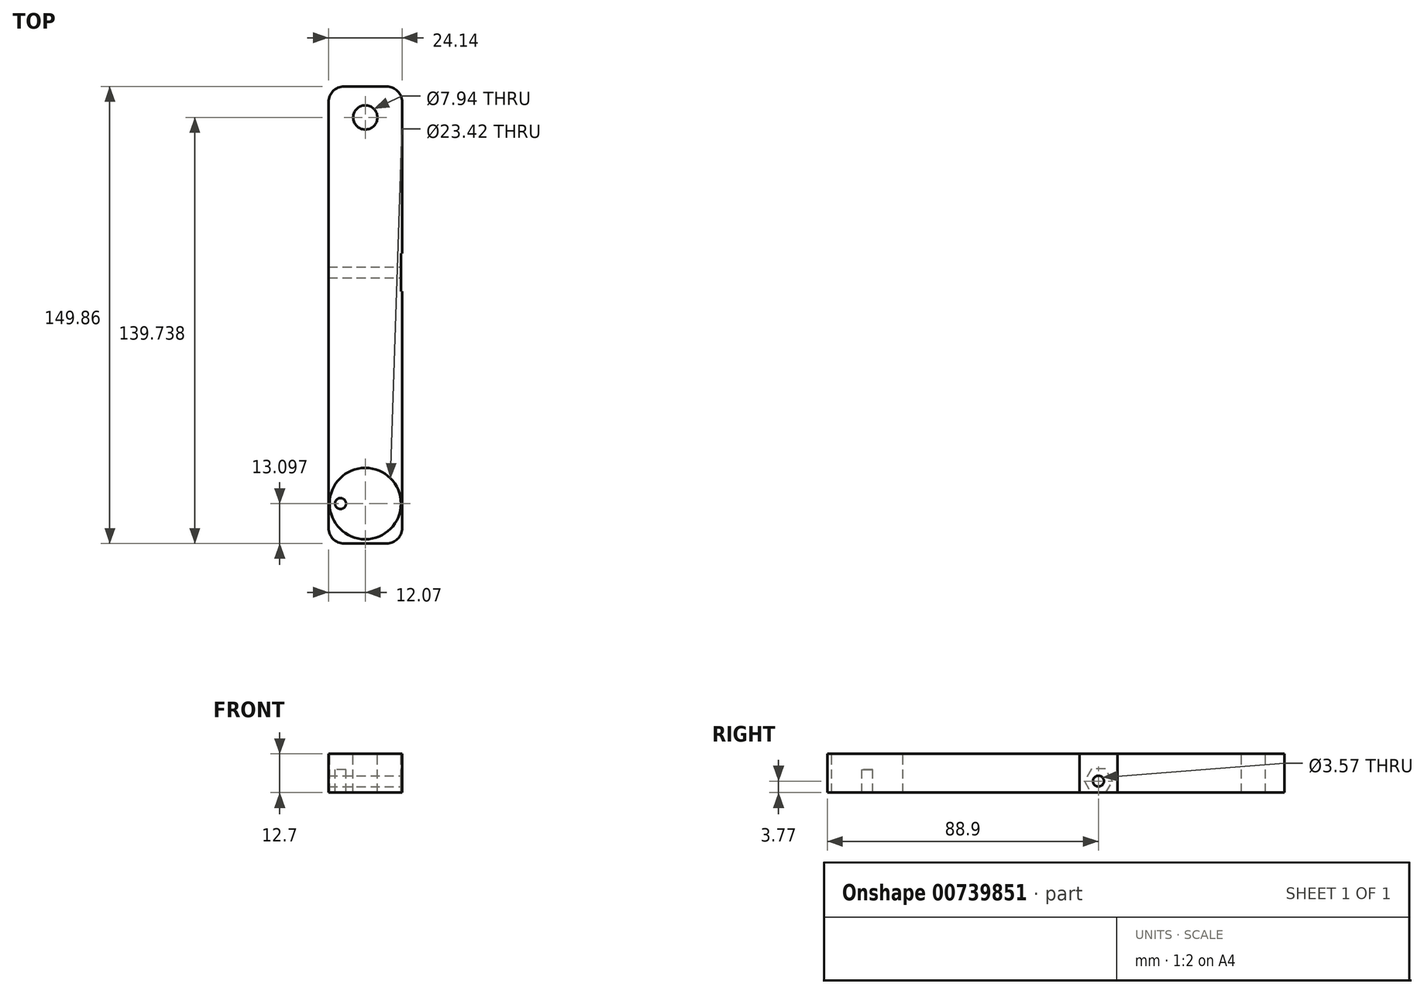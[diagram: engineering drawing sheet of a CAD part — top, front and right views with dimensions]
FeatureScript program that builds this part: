
annotation { "Feature Type Name" : "Feature", "Feature Type Description" : "" }
export const myFeature = defineFeature(function(context is Context, id is Id, definition is map)
    precondition{}
    {
        {
            var Q0;
            Q0=qCreatedBy(makeId("Top.planeOp"),FACE);
            var sketch = newSketch(context, id + "F0", { "sketchPlane" : qUnion([Q0])});
            skLineSegment(sketch, "E0.bottom", {"start": v(12.07, -88.9) * mm, "end": v(-12.06, -88.9) * mm});
            skLineSegment(sketch, "E0.top", {"start": v(12.06, 60.96) * mm, "end": v(-12.07, 60.96) * mm});
            skLineSegment(sketch, "E0.left", {"start": v(12.07, -88.9) * mm, "end": v(12.06, 60.96) * mm});
            skLineSegment(sketch, "E0.right", {"start": v(-12.06, -88.9) * mm, "end": v(-12.07, 60.96) * mm});
            skSolve(sketch);
        }
        {
            var Q0;
            Q0=makeQuery(id+"F0.imprint","IMPRINT",FACE,{"disambiguationData":[TD([[makeQuery(id+"F0.imprint","IMPRINT",EDGE,{"derivedFrom":sQuery(id+"F0.wireOp",EDGE,"E0.bottom")}),-1.0]])]});
            extrude(context, id + "F1", {"entities" : qUnion([Q0]), "depth" : 12.7 * mm, "offsetDistance" : 25.4 * mm});
        }
        {
            var Q0;
            Q0=makeQuery(id+"F1.opExtrude","SWEPT_FACE",FACE,{"disambiguationData":[OSD([sQuery(id+"F0.wireOp",EDGE,"E0.left")])]});
            var sketch = newSketch(context, id + "F2", { "sketchPlane" : qUnion([Q0])});
            skLineSegment(sketch, "E1.bottom", {"start": v(6.22, 12.7) * mm, "end": v(-6.22, 12.7) * mm});
            skLineSegment(sketch, "E1.top", {"start": v(6.22, -7.62) * mm, "end": v(-6.22, -7.62) * mm});
            skLineSegment(sketch, "E1.left", {"start": v(6.22, 12.7) * mm, "end": v(6.22, -7.62) * mm});
            skLineSegment(sketch, "E1.right", {"start": v(-6.22, 12.7) * mm, "end": v(-6.22, -7.62) * mm});
            skSolve(sketch);
        }
        {
            var Q0;
            Q0 = qSketchRegion(id + "F2", true);
            extrude(context, id + "F3", {"entities" : qUnion([Q0]), "operationType" : NewBodyOperationType.REMOVE, "oppositeDirection" : true, "depth" : 0.3 * mm, "offsetDistance" : 25.4 * mm});
        }
        {
            var Q0;
            Q0=makeQuery(id+"F1.opExtrude","CAP_FACE",FACE,{"disambiguationData":[OSD([sQuery(id+"F0.wireOp",EDGE,"E0.bottom"),sQuery(id+"F0.wireOp",EDGE,"E0.top"),sQuery(id+"F0.wireOp",EDGE,"E0.left"),sQuery(id+"F0.wireOp",EDGE,"E0.right")])],"isStart":false});
            var sketch = newSketch(context, id + "F4", { "sketchPlane" : qUnion([Q0])});
            skCircle(sketch, "E2", {"center": v(1.59, 51.33) * mm, "radius": 1.59 * mm, "construction": true});
            skCircle(sketch, "E3.MirrorC", {"center": v(-1.59, 51.33) * mm, "radius": 1.59 * mm, "construction": true});
            skCircle(sketch, "E4", {"center": v(0, 48.58) * mm, "radius": 1.59 * mm, "construction": true});
            skCircle(sketch, "E5", {"center": v(0, 50.84) * mm, "radius": 3.97 * mm});
            skSolve(sketch);
        }
        {
            var Q0;
            Q0 = qSketchRegion(id + "F4", true);
            extrude(context, id + "F5", {"entities" : qUnion([Q0]), "operationType" : NewBodyOperationType.REMOVE, "oppositeDirection" : true, "depth" : 25.4 * mm, "offsetDistance" : 25.4 * mm});
        }
        {
            var Q0;
            Q0=makeQuery(id+"F1.opExtrude","CAP_FACE",FACE,{"disambiguationData":[OSD([sQuery(id+"F0.wireOp",EDGE,"E0.bottom"),sQuery(id+"F0.wireOp",EDGE,"E0.top"),sQuery(id+"F0.wireOp",EDGE,"E0.left"),sQuery(id+"F0.wireOp",EDGE,"E0.right")])],"isStart":false});
            var sketch = newSketch(context, id + "F6", { "sketchPlane" : qUnion([Q0])});
            skCircle(sketch, "E6", {"center": v(0, -75.8) * mm, "radius": 11.7 * mm});
            skCircle(sketch, "E7", {"center": v(0, 0) * mm, "radius": 44.45 * mm, "construction": true});
            skLineSegment(sketch, "E8", {"start": v(0, -44.45) * mm, "end": v(60.85, -44.45) * mm, "construction": true});
            skSolve(sketch);
        }
        {
            var Q0;
            Q0=makeQuery(id+"F3.boolean.opBoolean","COPY",FACE,{"derivedFrom":makeQuery(id+"F3.opExtrude","CAP_FACE",FACE,{"disambiguationData":[OSD([sQuery(id+"F2.wireOp",EDGE,"E1.bottom"),sQuery(id+"F2.wireOp",EDGE,"E1.top"),sQuery(id+"F2.wireOp",EDGE,"E1.left"),sQuery(id+"F2.wireOp",EDGE,"E1.right")])],"isStart":false})});
            var sketch = newSketch(context, id + "F7", { "sketchPlane" : qUnion([Q0])});
            skCircle(sketch, "E9", {"center": v(0, 3.77) * mm, "radius": 1.79 * mm});
            skSolve(sketch);
        }
        {
            var Q0;
            Q0=makeQuery(id+"F7.imprint","IMPRINT",FACE,{"disambiguationData":[TD([[makeQuery(id+"F7.imprint","IMPRINT",EDGE,{"derivedFrom":sQuery(id+"F7.wireOp",EDGE,"E9")}),1.0]])]});
            extrude(context, id + "F8", {"entities" : qUnion([Q0]), "operationType" : NewBodyOperationType.REMOVE, "oppositeDirection" : true, "depth" : 25.4 * mm, "offsetDistance" : 25.4 * mm});
        }
        {
            var Q0;
            Q0=makeQuery(id+"F6.imprint","IMPRINT",FACE,{"disambiguationData":[TD([[makeQuery(id+"F6.imprint","IMPRINT",EDGE,{"derivedFrom":sQuery(id+"F6.wireOp",EDGE,"E6")}),1.0]])]});
            extrude(context, id + "F9", {"entities" : qUnion([Q0]), "operationType" : NewBodyOperationType.REMOVE, "oppositeDirection" : true, "depth" : 5.16 * mm, "offsetDistance" : 25.4 * mm});
        }
        {
            var Q0;
            Q0=makeQuery(id+"F9.boolean.opBoolean","COPY",FACE,{"derivedFrom":makeQuery(id+"F9.opExtrude","CAP_FACE",FACE,{"disambiguationData":[OSD([sQuery(id+"F6.wireOp",EDGE,"E6")])],"isStart":false})});
            var sketch = newSketch(context, id + "F10", { "sketchPlane" : qUnion([Q0])});
            skCircle(sketch, "E10", {"center": v(0, -75.8) * mm, "radius": 5.36 * mm});
            skSolve(sketch);
        }
        {
            var Q0;
            Q0 = qSketchRegion(id + "F10", true);
            extrude(context, id + "F11", {"entities" : qUnion([Q0]), "operationType" : NewBodyOperationType.REMOVE, "oppositeDirection" : true, "depth" : 25.4 * mm, "offsetDistance" : 25.4 * mm});
        }
        {
            var Q0;
            Q0=makeQuery(id+"F9.boolean.opBoolean","COPY",FACE,{"derivedFrom":makeQuery(id+"F9.opExtrude","CAP_FACE",FACE,{"disambiguationData":[OSD([sQuery(id+"F6.wireOp",EDGE,"E6")])],"isStart":false})});
            var sketch = newSketch(context, id + "F12", { "sketchPlane" : qUnion([Q0])});
            skCircle(sketch, "E11", {"center": v(8.14, -75.8) * mm, "radius": 1.8 * mm});
            skCircle(sketch, "E12.MirrorC", {"center": v(-8.14, -75.8) * mm, "radius": 1.8 * mm});
            skSolve(sketch);
        }
        {
            var Q0;
            Q0=makeQuery(id+"F12.imprint","IMPRINT",FACE,{"disambiguationData":[TD([[makeQuery(id+"F12.imprint","IMPRINT",EDGE,{"derivedFrom":sQuery(id+"F12.wireOp",EDGE,"E12.MirrorC")}),-1.0]])]});
            var Q1;
            Q1=makeQuery(id+"F12.imprint","IMPRINT",FACE,{"disambiguationData":[TD([[makeQuery(id+"F12.imprint","IMPRINT",EDGE,{"derivedFrom":sQuery(id+"F12.wireOp",EDGE,"E11")}),1.0]])]});
            var Q2;
            Q2=sQuery(id+"F12.wireOp",EDGE,"41002950-bd81-4fee-9a7b-5424229f296a0.MirrorC");
            var Q3;
            Q3=sQuery(id+"F12.wireOp",EDGE,"yZuGAu91-upIX-8ufI-HUdk-bfkT7uTKKsAl");
            extrude(context, id + "F13", {"entities" : qUnion([Q0, Q1]), "operationType" : NewBodyOperationType.REMOVE, "surfaceEntities" : qUnion([Q2, Q3]), "oppositeDirection" : true, "depth" : 25.4 * mm, "offsetDistance" : 25.4 * mm});
        }
        {
            var Q0;
            Q0=makeQuery(id+"F1.opExtrude","SWEPT_EDGE",EDGE,{"disambiguationData":[OSD([sQuery(id+"F0.wireOp",EDGE,"E0.bottom"),sQuery(id+"F0.wireOp",EDGE,"E0.right")])]});
            var Q1;
            Q1=makeQuery(id+"F1.opExtrude","SWEPT_EDGE",EDGE,{"disambiguationData":[OSD([sQuery(id+"F0.wireOp",EDGE,"E0.bottom"),sQuery(id+"F0.wireOp",EDGE,"E0.left")])]});
            var Q2;
            Q2=makeQuery(id+"F1.opExtrude","SWEPT_EDGE",EDGE,{"disambiguationData":[OSD([sQuery(id+"F0.wireOp",EDGE,"E0.top"),sQuery(id+"F0.wireOp",EDGE,"E0.right")])]});
            var Q3;
            Q3=makeQuery(id+"F1.opExtrude","SWEPT_EDGE",EDGE,{"disambiguationData":[OSD([sQuery(id+"F0.wireOp",EDGE,"E0.top"),sQuery(id+"F0.wireOp",EDGE,"E0.left")])]});
            fillet(context, id + "F14", {"entities" : qUnion([Q0, Q1, Q2, Q3]), "radius" : 5.08 * mm, "tangentPropagation" : true, "allowEdgeOverflow" : false});
        }
        {
            var Q0;
            Q0=makeQuery(id+"F1.opExtrude","SWEPT_FACE",FACE,{"disambiguationData":[OSD([sQuery(id+"F0.wireOp",EDGE,"E0.right")])]});
            var sketch = newSketch(context, id + "F15", { "sketchPlane" : qUnion([Q0])});
            skCircle(sketch, "E13.cCircle", {"center": v(0, 3.77) * mm, "radius": 3.97 * mm, "construction": true});
            skLineSegment(sketch, "E13.0", {"start": v(-2.3, 7.74) * mm, "end": v(2.3, 7.74) * mm});
            skLineSegment(sketch, "E13.1", {"start": v(2.3, 7.74) * mm, "end": v(4.58, 3.77) * mm});
            skLineSegment(sketch, "E13.2", {"start": v(4.58, 3.77) * mm, "end": v(2.3, -0.2) * mm});
            skLineSegment(sketch, "E13.3", {"start": v(2.3, -0.2) * mm, "end": v(-2.3, -0.2) * mm});
            skLineSegment(sketch, "E13.4", {"start": v(-2.3, -0.2) * mm, "end": v(-4.58, 3.77) * mm});
            skLineSegment(sketch, "E13.5", {"start": v(-4.58, 3.77) * mm, "end": v(-2.3, 7.74) * mm});
            skPoint(sketch, "E13.0.midPoint", {"position": v(0, 7.74) * mm});
            skSolve(sketch);
        }
        {
            var Q0;
            Q0 = qSketchRegion(id + "F15", true);
            extrude(context, id + "F16", {"entities" : qUnion([Q0]), "operationType" : NewBodyOperationType.REMOVE, "oppositeDirection" : true, "depth" : 7 / 1625.6 * mm, "offsetDistance" : 25.4 * mm});
        }
    });
